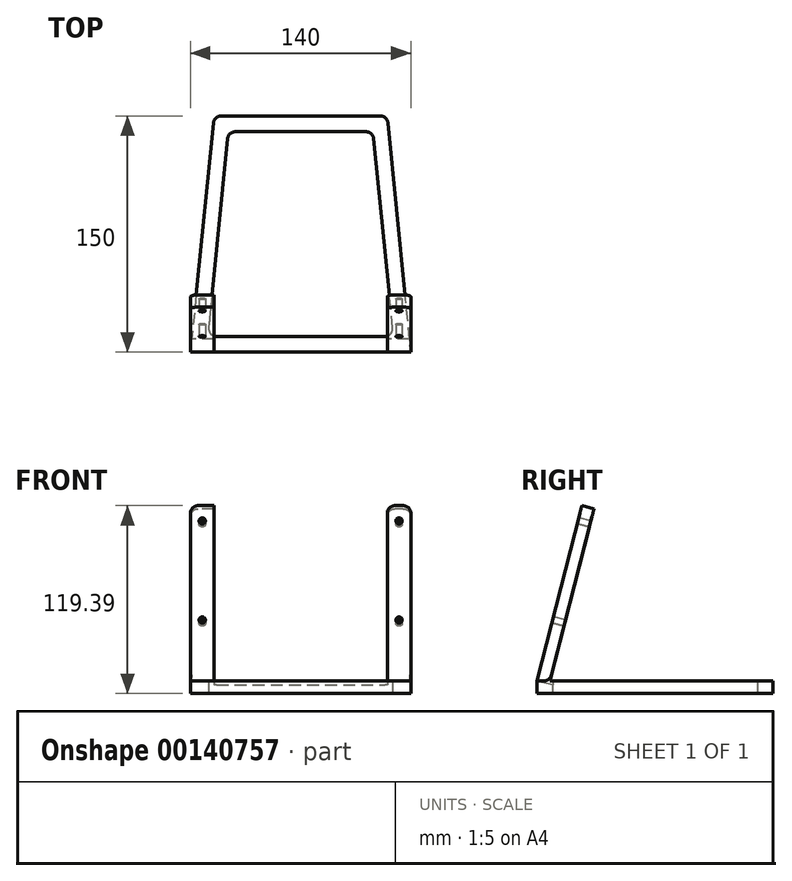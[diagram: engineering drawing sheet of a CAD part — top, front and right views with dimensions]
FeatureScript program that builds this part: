
annotation { "Feature Type Name" : "Feature", "Feature Type Description" : "" }
export const myFeature = defineFeature(function(context is Context, id is Id, definition is map)
    precondition{}
    {
        {
            var Q0;
            Q0=qCreatedBy(makeId("Top.planeOp"),FACE);
            var sketch = newSketch(context, id + "F0", { "sketchPlane" : qUnion([Q0])});
            skLineSegment(sketch, "E0", {"start": v(-70, -46.9) * mm, "end": v(70, -46.9) * mm});
            skLineSegment(sketch, "E1", {"start": v(70, -46.9) * mm, "end": v(55.45, 98.6) * mm});
            skLineSegment(sketch, "E2", {"start": v(50.48, 103.1) * mm, "end": v(-50.48, 103.1) * mm});
            skLineSegment(sketch, "E3", {"start": v(-55.45, 98.6) * mm, "end": v(-70, -46.9) * mm});
            skPoint(sketch, "E4.visualSharp", {"position": v(-55, 103.1) * mm});
            skArc(sketch, "E4.filletArc", {"start": v(-50.48, 103.1) * mm, "mid": v(-53.83, 101.81) * mm, "end": v(-55.45, 98.6) * mm});
            skPoint(sketch, "E5.visualSharp", {"position": v(55, 103.1) * mm});
            skArc(sketch, "E5.filletArc", {"start": v(55.45, 98.6) * mm, "mid": v(53.83, 101.81) * mm, "end": v(50.48, 103.1) * mm});
            skLineSegment(sketch, "E6.0", {"start": v(41.43, 93.1) * mm, "end": v(-41.43, 93.1) * mm});
            skLineSegment(sketch, "E6.1", {"start": v(58.4, -31.4) * mm, "end": v(46.4, 88.6) * mm});
            skLineSegment(sketch, "E6.2", {"start": v(-53.43, -36.9) * mm, "end": v(53.43, -36.9) * mm});
            skLineSegment(sketch, "E6.3", {"start": v(-46.4, 88.6) * mm, "end": v(-58.4, -31.4) * mm});
            skPoint(sketch, "E7.visualSharp", {"position": v(-45.95, 93.1) * mm});
            skArc(sketch, "E7.filletArc", {"start": v(-41.43, 93.1) * mm, "mid": v(-44.78, 91.81) * mm, "end": v(-46.4, 88.6) * mm});
            skPoint(sketch, "E8.visualSharp", {"position": v(45.95, 93.1) * mm});
            skArc(sketch, "E8.filletArc", {"start": v(46.4, 88.6) * mm, "mid": v(44.78, 91.81) * mm, "end": v(41.43, 93.1) * mm});
            skPoint(sketch, "E9.visualSharp", {"position": v(58.95, -36.9) * mm});
            skArc(sketch, "E9.filletArc", {"start": v(53.43, -36.9) * mm, "mid": v(57.13, -35.25) * mm, "end": v(58.4, -31.4) * mm});
            skPoint(sketch, "E10.visualSharp", {"position": v(-58.95, -36.9) * mm});
            skArc(sketch, "E10.filletArc", {"start": v(-58.4, -31.4) * mm, "mid": v(-57.13, -35.25) * mm, "end": v(-53.43, -36.9) * mm});
            skSolve(sketch);
        }
        {
            var Q0;
            Q0=makeQuery(id+"F0.imprint","IMPRINT",FACE,{"disambiguationData":[TD([[makeQuery(id+"F0.imprint","IMPRINT",EDGE,{"derivedFrom":sQuery(id+"F0.wireOp",EDGE,"E0")}),1.0]])]});
            extrude(context, id + "F1", {"entities" : qUnion([Q0]), "depth" : 8 * mm});
        }
        {
            var Q0;
            Q0=qCreatedBy(makeId("Right.planeOp"),FACE);
            var sketch = newSketch(context, id + "F2", { "sketchPlane" : qUnion([Q0])});
            skLineSegment(sketch, "E11", {"start": v(-46.9, 8) * mm, "end": v(-18.3, 119.4) * mm});
            skLineSegment(sketch, "E12", {"start": v(-18.3, 119.4) * mm, "end": v(-10.56, 117.4) * mm});
            skLineSegment(sketch, "E13", {"start": v(-10.56, 117.4) * mm, "end": v(-35.43, 20.49) * mm});
            skPoint(sketch, "E14.newPointB", {"position": v(-46.9, 8) * mm});
            skLineSegment(sketch, "E15", {"start": v(-35.43, 20.49) * mm, "end": v(-38.63, 8) * mm});
            skLineSegment(sketch, "E16", {"start": v(-38.63, 8) * mm, "end": v(-46.9, 8) * mm});
            skPoint(sketch, "E17.0.end.orphan", {"position": v(98.6, 8) * mm});
            skPoint(sketch, "E17.0.start.orphan", {"position": v(-25.74, 8) * mm});
            skSolve(sketch);
        }
        {
            var Q0;
            Q0=makeQuery(id+"F2.imprint","IMPRINT",FACE,{"disambiguationData":[TD([[makeQuery(id+"F2.imprint","IMPRINT",EDGE,{"derivedFrom":sQuery(id+"F2.wireOp",EDGE,"E11")}),-1.0]])]});
            extrude(context, id + "F3", {"entities" : qUnion([Q0]), "operationType" : NewBodyOperationType.ADD, "depth" : 70 * mm, "hasSecondDirection" : true, "secondDirectionOppositeDirection" : true, "secondDirectionDepth" : 70 * mm});
        }
        {
            var Q0;
            Q0=makeQuery(id+"F3.opExtrude","SWEPT_FACE",FACE,{"disambiguationData":[OSD([sQuery(id+"F2.wireOp",EDGE,"E11")])]});
            var sketch = newSketch(context, id + "F4", { "sketchPlane" : qUnion([Q0])});
            skLineSegment(sketch, "E18.bottom", {"start": v(62.5, 36.1) * mm, "end": v(-62.5, 36.1) * mm, "construction": true});
            skLineSegment(sketch, "E18.top", {"start": v(62.5, 101.1) * mm, "end": v(-62.5, 101.1) * mm, "construction": true});
            skLineSegment(sketch, "E18.left", {"start": v(62.5, 36.1) * mm, "end": v(62.5, 101.1) * mm, "construction": true});
            skLineSegment(sketch, "E18.right", {"start": v(-62.5, 36.1) * mm, "end": v(-62.5, 101.1) * mm, "construction": true});
            skPoint(sketch, "E18.middle", {"position": v(0, 68.6) * mm});
            skPoint(sketch, "E18.middle.positionSnap0", {"position": v(0, 111.1) * mm});
            skPoint(sketch, "E18.centerSnap0", {"position": v(0, 111.1) * mm});
            skCircle(sketch, "E19", {"center": v(-62.5, 101.1) * mm, "radius": 2 * mm});
            skCircle(sketch, "E20", {"center": v(62.5, 101.1) * mm, "radius": 2 * mm});
            skCircle(sketch, "E21", {"center": v(-62.5, 36.1) * mm, "radius": 2 * mm});
            skCircle(sketch, "E22", {"center": v(62.5, 36.1) * mm, "radius": 2 * mm});
            skLineSegment(sketch, "E23.bottom", {"start": v(-55, 111.1) * mm, "end": v(55, 111.1) * mm});
            skLineSegment(sketch, "E23.top", {"start": v(-55, -3.9) * mm, "end": v(55, -3.9) * mm});
            skLineSegment(sketch, "E23.left", {"start": v(-55, 111.1) * mm, "end": v(-55, -3.9) * mm});
            skLineSegment(sketch, "E23.right", {"start": v(55, 111.1) * mm, "end": v(55, -3.9) * mm});
            skSolve(sketch);
        }
        {
            var Q0;
            Q0=makeQuery(id+"F4.imprint","IMPRINT",FACE,{"disambiguationData":[TD([[makeQuery(id+"F4.imprint","IMPRINT",EDGE,{"derivedFrom":sQuery(id+"F4.wireOp",EDGE,"E23.bottom")}),1.0]])]});
            var Q1;
            Q1=makeQuery(id+"F4.imprint","IMPRINT",FACE,{"disambiguationData":[TD([[makeQuery(id+"F4.imprint","IMPRINT",EDGE,{"derivedFrom":sQuery(id+"F4.wireOp",EDGE,"E19")}),1.0]])]});
            var Q2;
            Q2=makeQuery(id+"F4.imprint","IMPRINT",FACE,{"disambiguationData":[TD([[makeQuery(id+"F4.imprint","IMPRINT",EDGE,{"derivedFrom":sQuery(id+"F4.wireOp",EDGE,"E21")}),1.0]])]});
            var Q3;
            Q3=makeQuery(id+"F4.imprint","IMPRINT",FACE,{"disambiguationData":[TD([[makeQuery(id+"F4.imprint","IMPRINT",EDGE,{"derivedFrom":sQuery(id+"F4.wireOp",EDGE,"E22")}),1.0]])]});
            var Q4;
            Q4=makeQuery(id+"F4.imprint","IMPRINT",FACE,{"disambiguationData":[TD([[makeQuery(id+"F4.imprint","IMPRINT",EDGE,{"derivedFrom":sQuery(id+"F4.wireOp",EDGE,"E20")}),1.0]])]});
            extrude(context, id + "F5", {"entities" : qUnion([Q0, Q1, Q2, Q3, Q4]), "operationType" : NewBodyOperationType.REMOVE, "endBound" : BoundingType.UP_TO_NEXT, "oppositeDirection" : true, "depth" : 25 * mm});
        }
        {
            var Q0;
            Q0=makeQuery(id+"F3.opExtrude","CAP_EDGE",EDGE,{"disambiguationData":[OSD([sQuery(id+"F2.wireOp",EDGE,"E12")])],"isStart":true});
            var Q1;
            Q1=makeQuery(id+"F5.boolean.opBoolean","COPY",EDGE,{"derivedFrom":makeQuery(id+"F5.opExtrude","SWEPT_EDGE",EDGE,{"disambiguationData":[OSD([sQuery(id+"F2.wireOp",EDGE,"E11"),sQuery(id+"F2.wireOp",EDGE,"E12"),sQuery(id+"F4.wireOp",EDGE,"E23.bottom"),sQuery(id+"F4.wireOp",EDGE,"E23.left")])]})});
            var Q2;
            Q2=makeQuery(id+"F5.boolean.opBoolean","COPY",EDGE,{"derivedFrom":makeQuery(id+"F5.opExtrude","SWEPT_EDGE",EDGE,{"disambiguationData":[OSD([sQuery(id+"F2.wireOp",EDGE,"E11"),sQuery(id+"F2.wireOp",EDGE,"E12"),sQuery(id+"F4.wireOp",EDGE,"E23.bottom"),sQuery(id+"F4.wireOp",EDGE,"E23.right")])]})});
            var Q3;
            Q3=makeQuery(id+"F3.opExtrude","CAP_EDGE",EDGE,{"disambiguationData":[OSD([sQuery(id+"F2.wireOp",EDGE,"E12")])],"isStart":false});
            fillet(context, id + "F6", {"entities" : qUnion([Q0, Q1, Q2, Q3]), "radius" : 5 * mm, "tangentPropagation" : true, "allowEdgeOverflow" : false});
        }
        {
            var Q0;
            {var subQ0=sQuery(id+"F2.wireOp",EDGE,"E16");var subQ1=sQuery(id+"F0.wireOp",EDGE,"E1");var subQ2=sQuery(id+"F2.wireOp",EDGE,"E15");var subQ3=makeQuery(id+"F3.opExtrude","SWEPT_FACE",FACE,{"disambiguationData":[OSD([sQuery(id+"F2.wireOp",EDGE,"E13"),subQ2])]});var subQ4=makeQuery(id+"F1.opExtrude","CAP_FACE",FACE,{"disambiguationData":[OSD([sQuery(id+"F0.wireOp",EDGE,"E0"),subQ1,sQuery(id+"F0.wireOp",EDGE,"E2"),sQuery(id+"F0.wireOp",EDGE,"E3"),sQuery(id+"F0.wireOp",EDGE,"E4.filletArc"),sQuery(id+"F0.wireOp",EDGE,"E5.filletArc"),sQuery(id+"F0.wireOp",EDGE,"E6.0"),sQuery(id+"F0.wireOp",EDGE,"E6.1"),sQuery(id+"F0.wireOp",EDGE,"E6.2"),sQuery(id+"F0.wireOp",EDGE,"E6.3"),sQuery(id+"F0.wireOp",EDGE,"E7.filletArc"),sQuery(id+"F0.wireOp",EDGE,"E8.filletArc"),sQuery(id+"F0.wireOp",EDGE,"E9.filletArc"),sQuery(id+"F0.wireOp",EDGE,"E10.filletArc")])],"isStart":false});Q0=makeQuery(id+"F5.boolean.opBoolean","SPLIT",EDGE,{"disambiguationData":[TD([makeQuery(id+"F1.opExtrude","SWEPT_FACE",FACE,{"disambiguationData":[OSD([subQ1])]})])],"derivedFrom":makeQuery(id+"F3.boolean.opBoolean","SPLIT",EDGE,{"disambiguationData":[topologyDisambiguationEdgeConnected([subQ4,subQ3])],"derivedFrom":makeQuery(id+"F3.opExtrude","SWEPT_EDGE",EDGE,{"disambiguationData":[OSD([subQ2,subQ0])]})})});}
            var Q1;
            {var subQ0=sQuery(id+"F2.wireOp",EDGE,"E16");var subQ1=sQuery(id+"F0.wireOp",EDGE,"E3");var subQ2=sQuery(id+"F2.wireOp",EDGE,"E15");var subQ3=makeQuery(id+"F3.opExtrude","SWEPT_FACE",FACE,{"disambiguationData":[OSD([sQuery(id+"F2.wireOp",EDGE,"E13"),subQ2])]});var subQ4=makeQuery(id+"F1.opExtrude","CAP_FACE",FACE,{"disambiguationData":[OSD([sQuery(id+"F0.wireOp",EDGE,"E0"),sQuery(id+"F0.wireOp",EDGE,"E1"),sQuery(id+"F0.wireOp",EDGE,"E2"),subQ1,sQuery(id+"F0.wireOp",EDGE,"E4.filletArc"),sQuery(id+"F0.wireOp",EDGE,"E5.filletArc"),sQuery(id+"F0.wireOp",EDGE,"E6.0"),sQuery(id+"F0.wireOp",EDGE,"E6.1"),sQuery(id+"F0.wireOp",EDGE,"E6.2"),sQuery(id+"F0.wireOp",EDGE,"E6.3"),sQuery(id+"F0.wireOp",EDGE,"E7.filletArc"),sQuery(id+"F0.wireOp",EDGE,"E8.filletArc"),sQuery(id+"F0.wireOp",EDGE,"E9.filletArc"),sQuery(id+"F0.wireOp",EDGE,"E10.filletArc")])],"isStart":false});Q1=makeQuery(id+"F5.boolean.opBoolean","SPLIT",EDGE,{"disambiguationData":[TD([makeQuery(id+"F1.opExtrude","SWEPT_FACE",FACE,{"disambiguationData":[OSD([subQ1])]})])],"derivedFrom":makeQuery(id+"F3.boolean.opBoolean","SPLIT",EDGE,{"disambiguationData":[topologyDisambiguationEdgeConnected([subQ4,subQ3])],"derivedFrom":makeQuery(id+"F3.opExtrude","SWEPT_EDGE",EDGE,{"disambiguationData":[OSD([subQ2,subQ0])]})})});}
            fillet(context, id + "F7", {"entities" : qUnion([Q0, Q1]), "radius" : 5 * mm, "tangentPropagation" : true, "allowEdgeOverflow" : false});
        }
    });
